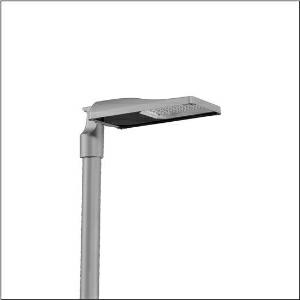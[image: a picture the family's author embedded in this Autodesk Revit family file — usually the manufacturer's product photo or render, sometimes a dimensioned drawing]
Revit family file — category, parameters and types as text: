
# Revit family: streetlight_sl_31_mini___st1_0a_5xh6d3ab08ja_7089
name_source: partatom
category: Lighting Fixtures
units: mm (PartAtom-declared; Revit-internal decimal feet)

## family parameters
Cut with Voids When Loaded = No
Host = Face
Light Source = No
Part Type = Normal
Room Calculation Point = No
Round Connector Dimension = Use Diameter
Shared = No

## types (1)
- --- (1 x LED, 12140 lm, 81.1 W, 3000K)
    Apparent Load = 81 VA
    CIE Flux Codes = 40 73 97 100 100
    Color Rendering = 70
    Color Temperature = 3000K
    Default Elevation = 1800 mm
    Description = Streetlight SL 31 mini Easy LST mast luminaire for post-top, side-entry; light control with lens of PMMA; light distribution: ST1.0a, direct asymmetric distribution, for standard-compliant lighting for roads and squares; LED: luminous flux: 12.140lm, light colour: 730, colour temperature: 3000K; luminous efficacy: 149,7lm/W; control: pre-setting: linear dimming characteristic, flexible luminous flux parameterisation, time-dependent luminous flux control, constant luminous flux control, power reduction, intelligent temperature release in ECG and LED module, overheat protection; luminaire housing, of diecast aluminium, Siteco® metallic grey (DB 702S), corrosivity category C5 high according to DIN EN ISO 12944; cover of toughened safety glass, transparent, opened without tools; mast flange of diecast aluminium, Siteco® metallic grey (DB 702S), spigot size: 76/60mm, mast flange included unmounted; with cable H07RN-F 3x 1.5mm², cable length: 10,5m, connection cable pre-assembled; mains connection: 220..240V, AC, 50/60Hz; power consumption (at start of service life): 81,1W / (at end of service life): 88,3W / (with reduced operation 50%): 36,4W; protection rating (complete): IP66; insulation class (complete): insulation class II (safety insulation); impact resistance: IK10; certification: CE, ENEC, ENEC+, VDE, UKCA; permissible operating ambient temperature for outdoor applications: -40..+50°C; packaging unit: 1 piece

Light Distribution: ST1.0a
    Height = 76 mm
    Lamp = 1 x LED
    Lamp Light Flux = 12140 lm
    Lamp Power = 81.1 W
    Lamp count = 1
    Length = 547 mm
    Luminous efficacy = 150 lm/W
    Manufacturer = Siteco
    ModVariant = No
    Model = 5XH6D3AB08JA
    Number of Poles = 1
    OnlyDefault = Yes
    Power Factor = 1
    Product Name = Streetlight SL 31 mini | ST1.0a
    Product group = mast luminaire | pylon top
    ProductGroupID = 6100
    Protection Class = Protection class II
    Protection Degree = IP 66
    RLX_Detail_Level = 1
    RLX_Emergency_Light_Flux = 0 lm
    RLX_Emergency_Type = 0
    RLX_Emergency_Type_DB = No
    RlxData = <blob elided: 39629 chars, md5=a70d26c1>
    Socket = socket
    Standby Power = 0 W
    System Light Flux = 12140 lm
    System Power = 81 W
    Type Comments = factory setting: luminous flux: 100 % | dim-lin: 254 | 860 mA
    Type Image = l_1300326.jpg
    URL = http://relux.com
    VarID = @adj_070957
    Voltage = 0 V
    Weight = 0.00 kg
    Width = 265 mm

## geometry (parser evidence)
native form markers: Blend x4, Sweep x9
no freeform markers — native parametric forms only
